# Revit family: 5LES26333RSQ75T,2T
name_source: partatom
category: Plumbing Fixtures
units: mm (PartAtom-declared; Revit-internal decimal feet)

## family parameters
Always vertical = Yes
Cut with Voids When Loaded = No
OmniClass Number = 23.45.05.14.17
OmniClass Title = Showers
Part Type = Normal
Room Calculation Point = No
Round Connector Dimension = Use Diameter
Shared = No
Work Plane-Based = No

## types (2) — shared parameters
Assembly Code = D2010710
Description = 8 in Tile, Traditional Bull-Nose Threshold
Keynote = 22 40 00.B3
Manufacturer = Best Bath Systems, Inc.
Type Comments = ADA Compliant
URL = http://www.best-bath.com
Unit Depth = 34"
Unit Width = 63"

## per-type parameters (varying)
| type | Threshold Height | Unit Height |
| 5LES26333RSQ75T | 3/4" | 81 1/4" |
| 5LES26333RSQ2T | 2" | 82 1/2" |

note: column(s) folded — value = type name in every type: Model

## geometry (parser evidence)
native form markers: Blend x21, Sweep x6
no freeform markers — native parametric forms only
